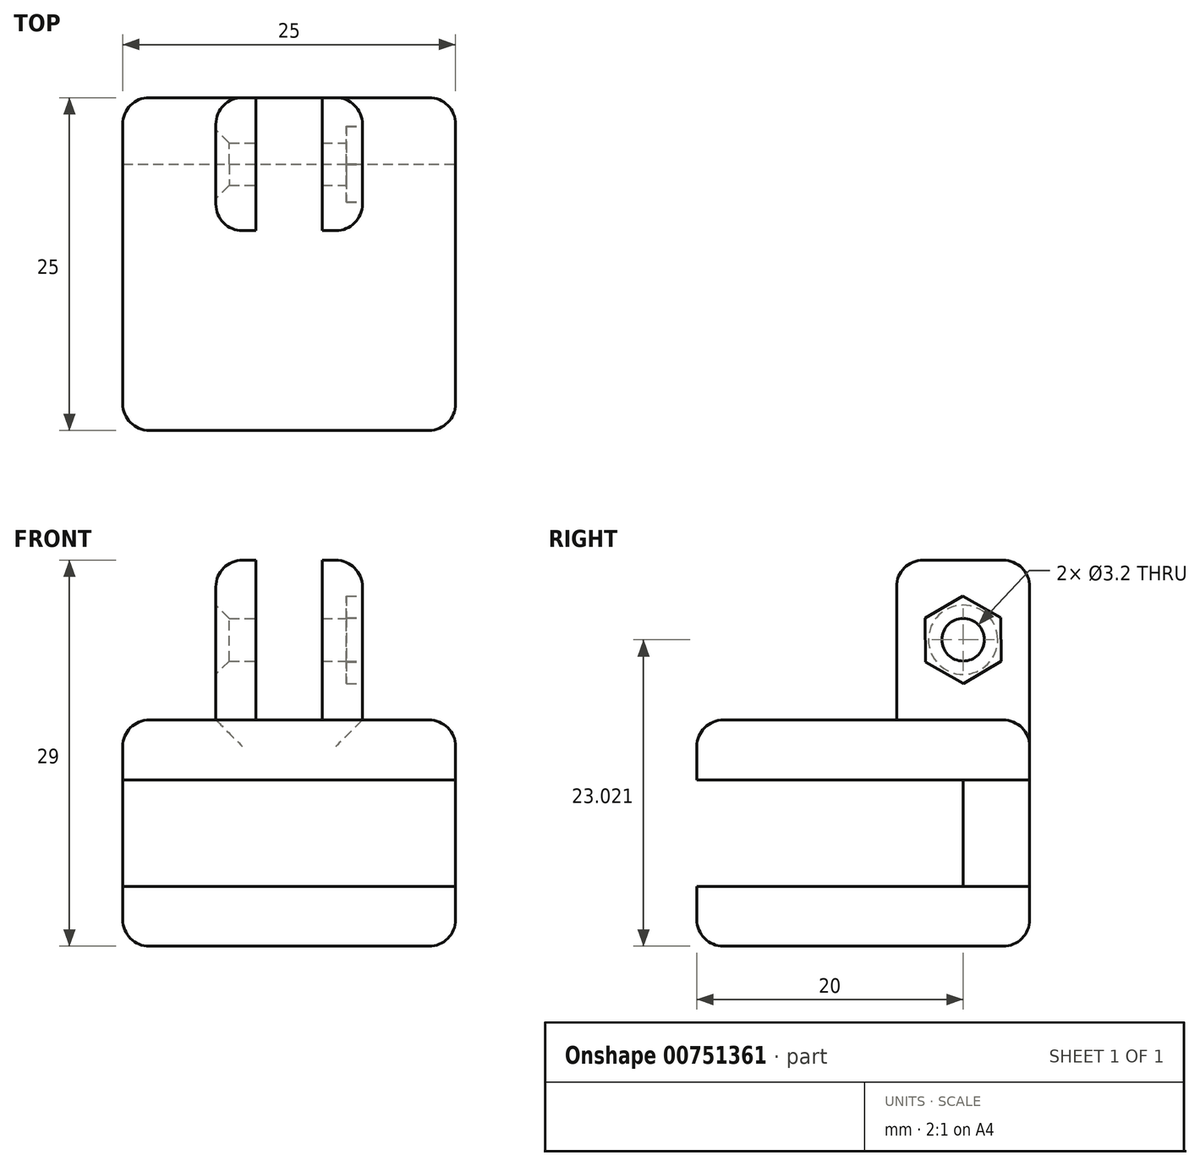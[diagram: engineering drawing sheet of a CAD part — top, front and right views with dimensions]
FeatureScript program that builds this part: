
annotation { "Feature Type Name" : "Feature", "Feature Type Description" : "" }
export const myFeature = defineFeature(function(context is Context, id is Id, definition is map)
    precondition{}
    {
        {
            var Q0;
            Q0=qCreatedBy(makeId("Front.planeOp"),FACE);
            var sketch = newSketch(context, id + "F0", { "sketchPlane" : qUnion([Q0])});
            skLineSegment(sketch, "E0.bottom", {"start": v(12.5, 8.5) * mm, "end": v(-12.5, 8.5) * mm});
            skLineSegment(sketch, "E0.top", {"start": v(12.5, -8.5) * mm, "end": v(-12.5, -8.5) * mm});
            skLineSegment(sketch, "E0.left", {"start": v(12.5, 8.5) * mm, "end": v(12.5, -8.5) * mm});
            skLineSegment(sketch, "E0.right", {"start": v(-12.5, 8.5) * mm, "end": v(-12.5, -8.5) * mm});
            skPoint(sketch, "E0.middle", {"position": v(0, 0) * mm});
            skLineSegment(sketch, "E1.bottom", {"start": v(-2.5, 20.5) * mm, "end": v(2.5, 20.5) * mm});
            skLineSegment(sketch, "E1.top", {"start": v(-2.5, 8.5) * mm, "end": v(2.5, 8.5) * mm});
            skLineSegment(sketch, "E1.left", {"start": v(-2.5, 20.5) * mm, "end": v(-2.5, 8.5) * mm});
            skLineSegment(sketch, "E1.right", {"start": v(2.5, 20.5) * mm, "end": v(2.5, 8.5) * mm});
            skLineSegment(sketch, "E2", {"start": v(0, 0) * mm, "end": v(0, 48.1) * mm, "construction": true});
            skPoint(sketch, "E2.endSnap0", {"position": v(0, 8.5) * mm});
            skLineSegment(sketch, "E3.bottom", {"start": v(-2.5, 8.5) * mm, "end": v(-5.5, 8.5) * mm});
            skLineSegment(sketch, "E3.top", {"start": v(-2.5, 20.5) * mm, "end": v(-5.5, 20.5) * mm});
            skLineSegment(sketch, "E3.left", {"start": v(-2.5, 8.5) * mm, "end": v(-2.5, 20.5) * mm});
            skLineSegment(sketch, "E3.right", {"start": v(-5.5, 8.5) * mm, "end": v(-5.5, 20.5) * mm});
            skLineSegment(sketch, "E4.MirrorCS", {"start": v(5.5, 8.5) * mm, "end": v(5.5, 20.5) * mm});
            skLineSegment(sketch, "E5.MirrorCS", {"start": v(2.5, 20.5) * mm, "end": v(5.5, 20.5) * mm});
            skLineSegment(sketch, "E6.MirrorCS", {"start": v(2.5, 8.5) * mm, "end": v(5.5, 8.5) * mm});
            skPoint(sketch, "E7.visualSharp", {"position": v(-12.5, -8.5) * mm});
            skLineSegment(sketch, "E7.filletArc", {"start": v(-12.5, -8.5) * mm, "end": v(-12.5, -8.5) * mm});
            skPoint(sketch, "E8.visualSharp", {"position": v(12.5, -8.5) * mm});
            skLineSegment(sketch, "E8.filletArc", {"start": v(12.5, -8.5) * mm, "end": v(12.5, -8.5) * mm});
            skPoint(sketch, "E9.visualSharp", {"position": v(-5.5, 20.5) * mm});
            skLineSegment(sketch, "E9.filletArc", {"start": v(-5.5, 20.5) * mm, "end": v(-5.5, 20.5) * mm});
            skPoint(sketch, "E10.visualSharp", {"position": v(5.5, 20.5) * mm});
            skLineSegment(sketch, "E10.filletArc", {"start": v(5.5, 20.5) * mm, "end": v(5.5, 20.5) * mm});
            skLineSegment(sketch, "E11.bottom", {"start": v(-12.5, 4) * mm, "end": v(12.5, 4) * mm});
            skLineSegment(sketch, "E11.top", {"start": v(-12.5, -4) * mm, "end": v(12.5, -4) * mm});
            skLineSegment(sketch, "E11.left", {"start": v(-12.5, 4) * mm, "end": v(-12.5, -4) * mm});
            skLineSegment(sketch, "E11.right", {"start": v(12.5, 4) * mm, "end": v(12.5, -4) * mm});
            skLineSegment(sketch, "E12", {"start": v(-5.5, 20.5) * mm, "end": v(5.5, 8.5) * mm, "construction": true});
            skLineSegment(sketch, "E13", {"start": v(5.5, 20.5) * mm, "end": v(-5.5, 8.5) * mm, "construction": true});
            skPoint(sketch, "E14", {"position": v(0, 14.5) * mm});
            skLineSegment(sketch, "E15", {"start": v(0, 14.5) * mm, "end": v(-5.5, 14.5) * mm, "construction": true});
            skPoint(sketch, "E16", {"position": v(-5.5, 14.5) * mm});
            skSolve(sketch);
        }
        {
            var Q0;
            {var subQ0=sQuery(id+"F0.wireOp",EDGE,"E0.top");Q0=makeQuery(id+"F0.imprint","IMPRINT",FACE,{"disambiguationData":[TD([[makeQuery(id+"F0.imprint","IMPRINT",EDGE,{"derivedFrom":subQ0}),-1.0]])]});}
            var Q1;
            {var subQ9=sQuery(id+"F0.wireOp",EDGE,"E11.bottom");Q1=makeQuery(id+"F0.imprint","IMPRINT",FACE,{"disambiguationData":[TD([[makeQuery(id+"F0.imprint","IMPRINT",EDGE,{"derivedFrom":subQ9}),1.0]])]});}
            extrude(context, id + "F1", {"entities" : qUnion([Q0, Q1]), "depth" : 25 * mm, "offsetDistance" : 25 * mm});
        }
        {
            var Q0;
            {var subQ0=sQuery(id+"F0.wireOp",EDGE,"E11.bottom");Q0=makeQuery(id+"F0.imprint","IMPRINT",FACE,{"disambiguationData":[TD([[makeQuery(id+"F0.imprint","IMPRINT",EDGE,{"derivedFrom":subQ0}),-1.0]])]});}
            extrude(context, id + "F2", {"entities" : qUnion([Q0]), "depth" : 5 * mm, "offsetDistance" : 25 * mm});
        }
        {
            var Q0;
            {var subQ0=sQuery(id+"F0.wireOp",EDGE,"E1.right");Q0=makeQuery(id+"F0.imprint","IMPRINT",FACE,{"disambiguationData":[TD([[makeQuery(id+"F0.imprint","IMPRINT",EDGE,{"derivedFrom":subQ0}),1.0]])]});}
            var Q1;
            {var subQ2=sQuery(id+"F0.wireOp",EDGE,"E1.left");Q1=makeQuery(id+"F0.imprint","IMPRINT",FACE,{"disambiguationData":[TD([[makeQuery(id+"F0.imprint","IMPRINT",EDGE,{"derivedFrom":subQ2}),-1.0]])]});}
            extrude(context, id + "F3", {"entities" : qUnion([Q0, Q1]), "operationType" : NewBodyOperationType.ADD, "depth" : 10 * mm, "offsetDistance" : 25 * mm});
        }
        {
            var Q0;
            Q0=qCreatedBy(makeId("Right.planeOp"),FACE);
            var sketch = newSketch(context, id + "F4", { "sketchPlane" : qUnion([Q0])});
            skLineSegment(sketch, "E17", {"start": v(0, 14.52) * mm, "end": v(-10, 14.52) * mm});
            skCircle(sketch, "E18", {"center": v(-5, 14.52) * mm, "radius": 1.6 * mm});
            skSolve(sketch);
        }
        {
            var Q0;
            {var subQ0=sQuery(id+"F4.wireOp",EDGE,"E18");var subQ1=sQuery(id+"F4.wireOp",EDGE,"E17");var subQ2=makeQuery(id+"F4.imprint","INTERSECT",VERTEX,{"disambiguationData":[OD(0.0)],"derivedFrom":[subQ1,subQ0]});Q0=makeQuery(id+"F4.imprint","IMPRINT",FACE,{"disambiguationData":[TD([[makeQuery(id+"F4.imprint","IMPRINT",EDGE,{"disambiguationData":[TD([[subQ2,1.0]])],"derivedFrom":subQ1}),-1.0]])]});}
            var Q1;
            {var subQ0=sQuery(id+"F4.wireOp",EDGE,"E18");var subQ1=sQuery(id+"F4.wireOp",EDGE,"E17");var subQ2=makeQuery(id+"F4.imprint","INTERSECT",VERTEX,{"disambiguationData":[OD(0.0)],"derivedFrom":[subQ1,subQ0]});Q1=makeQuery(id+"F4.imprint","IMPRINT",FACE,{"disambiguationData":[TD([[makeQuery(id+"F4.imprint","IMPRINT",EDGE,{"disambiguationData":[TD([[subQ2,1.0]])],"derivedFrom":subQ1}),1.0]])]});}
            var Q2;
            Q2=sQuery(id+"F4.wireOp",EDGE,"E18");
            extrude(context, id + "F5", {"entities" : qUnion([Q0, Q1]), "operationType" : NewBodyOperationType.REMOVE, "surfaceEntities" : qUnion([Q2]), "oppositeDirection" : true, "depth" : 11.2 * mm, "offsetDistance" : 25 * mm, "hasSecondDirection" : true, "secondDirectionOppositeDirection" : false, "secondDirectionDepth" : 25 * mm});
        }
        {
            var Q0;
            Q0=makeQuery(id+"F3.opExtrude","SWEPT_EDGE",EDGE,{"disambiguationData":[OSD([sQuery(id+"F0.wireOp",EDGE,"E3.top"),sQuery(id+"F0.wireOp",EDGE,"E3.right")])]});
            var Q1;
            Q1=makeQuery(id+"F1.opExtrude","CAP_EDGE",EDGE,{"disambiguationData":[OSD([sQuery(id+"F0.wireOp",EDGE,"E0.bottom")])],"isStart":false});
            var Q2;
            Q2=makeQuery(id+"F1.opExtrude","SWEPT_EDGE",EDGE,{"disambiguationData":[OSD([sQuery(id+"F0.wireOp",EDGE,"E0.bottom"),sQuery(id+"F0.wireOp",EDGE,"E0.left")])]});
            var Q3;
            Q3=makeQuery(id+"F1.opExtrude","SWEPT_EDGE",EDGE,{"disambiguationData":[OSD([sQuery(id+"F0.wireOp",EDGE,"E0.bottom"),sQuery(id+"F0.wireOp",EDGE,"E0.right")])]});
            var Q4;
            {var subQ0=sQuery(id+"F0.wireOp",EDGE,"E0.right");Q4=makeQuery(id+"F1.opExtrude","CAP_EDGE",EDGE,{"disambiguationData":[OSD([subQ0]),TDD([makeQuery(id+"F0.imprint","IMPRINT",EDGE,{"disambiguationData":[TD([[makeQuery(id+"F0.imprint","INTERSECT",VERTEX,{"derivedFrom":[subQ0,sQuery(id+"F0.wireOp",EDGE,"E11.bottom")]}),1.0]])],"derivedFrom":subQ0})])],"isStart":true});}
            var Q5;
            {var subQ0=sQuery(id+"F0.wireOp",EDGE,"E0.bottom");var subQ3=sQuery(id+"F0.wireOp",EDGE,"E3.right");Q5=makeQuery(id+"F3.boolean.opBoolean","SPLIT",EDGE,{"disambiguationData":[TD([makeQuery(id+"F3.opExtrude","SWEPT_FACE",FACE,{"disambiguationData":[OSD([subQ3])]})])],"derivedFrom":makeQuery(id+"F1.opExtrude","CAP_EDGE",EDGE,{"disambiguationData":[OSD([subQ0])],"isStart":true})});}
            var Q6;
            {var subQ0=sQuery(id+"F0.wireOp",EDGE,"E4.MirrorCS");var subQ1=sQuery(id+"F0.wireOp",EDGE,"E0.bottom");Q6=makeQuery(id+"F3.boolean.opBoolean","SPLIT",EDGE,{"disambiguationData":[TD([makeQuery(id+"F3.opExtrude","SWEPT_FACE",FACE,{"disambiguationData":[OSD([subQ0])]})])],"derivedFrom":makeQuery(id+"F1.opExtrude","CAP_EDGE",EDGE,{"disambiguationData":[OSD([subQ1])],"isStart":true})});}
            var Q7;
            Q7=makeQuery(id+"F2.opExtrude","CAP_EDGE",EDGE,{"disambiguationData":[OSD([sQuery(id+"F0.wireOp",EDGE,"E0.left")])],"isStart":true});
            var Q8;
            {var subQ0=sQuery(id+"F0.wireOp",EDGE,"E0.left");Q8=makeQuery(id+"F1.opExtrude","CAP_EDGE",EDGE,{"disambiguationData":[OSD([subQ0]),TDD([makeQuery(id+"F0.imprint","IMPRINT",EDGE,{"disambiguationData":[TD([[makeQuery(id+"F0.imprint","INTERSECT",VERTEX,{"derivedFrom":[subQ0,sQuery(id+"F0.wireOp",EDGE,"E11.bottom")]}),1.0]])],"derivedFrom":subQ0})])],"isStart":true});}
            var Q9;
            {var subQ0=sQuery(id+"F0.wireOp",EDGE,"E0.left");Q9=makeQuery(id+"F1.opExtrude","CAP_EDGE",EDGE,{"disambiguationData":[OSD([subQ0]),TDD([makeQuery(id+"F0.imprint","IMPRINT",EDGE,{"disambiguationData":[TD([[makeQuery(id+"F0.imprint","INTERSECT",VERTEX,{"derivedFrom":[sQuery(id+"F0.wireOp",EDGE,"E0.top"),subQ0]}),1.0]])],"derivedFrom":subQ0})])],"isStart":true});}
            var Q10;
            Q10=makeQuery(id+"F2.opExtrude","CAP_EDGE",EDGE,{"disambiguationData":[OSD([sQuery(id+"F0.wireOp",EDGE,"E0.right")])],"isStart":true});
            var Q11;
            {var subQ0=sQuery(id+"F0.wireOp",EDGE,"E0.right");Q11=makeQuery(id+"F1.opExtrude","CAP_EDGE",EDGE,{"disambiguationData":[OSD([subQ0]),TDD([makeQuery(id+"F0.imprint","IMPRINT",EDGE,{"disambiguationData":[TD([[makeQuery(id+"F0.imprint","INTERSECT",VERTEX,{"derivedFrom":[sQuery(id+"F0.wireOp",EDGE,"E0.top"),subQ0]}),1.0]])],"derivedFrom":subQ0})])],"isStart":true});}
            var Q12;
            Q12=makeQuery(id+"F1.opExtrude","CAP_EDGE",EDGE,{"disambiguationData":[OSD([sQuery(id+"F0.wireOp",EDGE,"E0.top")])],"isStart":true});
            var Q13;
            Q13=makeQuery(id+"F1.opExtrude","SWEPT_EDGE",EDGE,{"disambiguationData":[OSD([sQuery(id+"F0.wireOp",EDGE,"E0.top"),sQuery(id+"F0.wireOp",EDGE,"E0.right")])]});
            var Q14;
            Q14=makeQuery(id+"F1.opExtrude","SWEPT_EDGE",EDGE,{"disambiguationData":[OSD([sQuery(id+"F0.wireOp",EDGE,"E0.top"),sQuery(id+"F0.wireOp",EDGE,"E0.left")])]});
            var Q15;
            Q15=makeQuery(id+"F3.opExtrude","CAP_EDGE",EDGE,{"disambiguationData":[OSD([sQuery(id+"F0.wireOp",EDGE,"E3.right")])],"isStart":true});
            var Q16;
            Q16=makeQuery(id+"F3.opExtrude","CAP_EDGE",EDGE,{"disambiguationData":[OSD([sQuery(id+"F0.wireOp",EDGE,"E3.right")])],"isStart":false});
            var Q17;
            Q17=makeQuery(id+"F3.opExtrude","CAP_EDGE",EDGE,{"disambiguationData":[OSD([sQuery(id+"F0.wireOp",EDGE,"E4.MirrorCS")])],"isStart":true});
            var Q18;
            Q18=makeQuery(id+"F3.opExtrude","CAP_EDGE",EDGE,{"disambiguationData":[OSD([sQuery(id+"F0.wireOp",EDGE,"E4.MirrorCS")])],"isStart":false});
            var Q19;
            {var subQ0=sQuery(id+"F0.wireOp",EDGE,"E0.left");Q19=makeQuery(id+"F1.opExtrude","CAP_EDGE",EDGE,{"disambiguationData":[OSD([subQ0]),TDD([makeQuery(id+"F0.imprint","IMPRINT",EDGE,{"disambiguationData":[TD([[makeQuery(id+"F0.imprint","INTERSECT",VERTEX,{"derivedFrom":[subQ0,sQuery(id+"F0.wireOp",EDGE,"E11.bottom")]}),1.0]])],"derivedFrom":subQ0})])],"isStart":false});}
            var Q20;
            {var subQ0=sQuery(id+"F0.wireOp",EDGE,"E0.right");Q20=makeQuery(id+"F1.opExtrude","CAP_EDGE",EDGE,{"disambiguationData":[OSD([subQ0]),TDD([makeQuery(id+"F0.imprint","IMPRINT",EDGE,{"disambiguationData":[TD([[makeQuery(id+"F0.imprint","INTERSECT",VERTEX,{"derivedFrom":[subQ0,sQuery(id+"F0.wireOp",EDGE,"E11.bottom")]}),1.0]])],"derivedFrom":subQ0})])],"isStart":false});}
            var Q21;
            Q21=makeQuery(id+"F1.opExtrude","CAP_EDGE",EDGE,{"disambiguationData":[OSD([sQuery(id+"F0.wireOp",EDGE,"E0.top")])],"isStart":false});
            var Q22;
            {var subQ0=sQuery(id+"F0.wireOp",EDGE,"E0.right");Q22=makeQuery(id+"F1.opExtrude","CAP_EDGE",EDGE,{"disambiguationData":[OSD([subQ0]),TDD([makeQuery(id+"F0.imprint","IMPRINT",EDGE,{"disambiguationData":[TD([[makeQuery(id+"F0.imprint","INTERSECT",VERTEX,{"derivedFrom":[sQuery(id+"F0.wireOp",EDGE,"E0.top"),subQ0]}),1.0]])],"derivedFrom":subQ0})])],"isStart":false});}
            var Q23;
            {var subQ0=sQuery(id+"F0.wireOp",EDGE,"E0.left");Q23=makeQuery(id+"F1.opExtrude","CAP_EDGE",EDGE,{"disambiguationData":[OSD([subQ0]),TDD([makeQuery(id+"F0.imprint","IMPRINT",EDGE,{"disambiguationData":[TD([[makeQuery(id+"F0.imprint","INTERSECT",VERTEX,{"derivedFrom":[sQuery(id+"F0.wireOp",EDGE,"E0.top"),subQ0]}),1.0]])],"derivedFrom":subQ0})])],"isStart":false});}
            var Q24;
            Q24=makeQuery(id+"F3.opExtrude","SWEPT_EDGE",EDGE,{"disambiguationData":[OSD([sQuery(id+"F0.wireOp",EDGE,"E4.MirrorCS"),sQuery(id+"F0.wireOp",EDGE,"E5.MirrorCS")])]});
            var Q25;
            Q25=makeQuery(id+"F3.opExtrude","CAP_EDGE",EDGE,{"disambiguationData":[OSD([sQuery(id+"F0.wireOp",EDGE,"E5.MirrorCS")])],"isStart":false});
            var Q26;
            Q26=makeQuery(id+"F3.opExtrude","CAP_EDGE",EDGE,{"disambiguationData":[OSD([sQuery(id+"F0.wireOp",EDGE,"E5.MirrorCS")])],"isStart":true});
            var Q27;
            Q27=makeQuery(id+"F3.opExtrude","CAP_EDGE",EDGE,{"disambiguationData":[OSD([sQuery(id+"F0.wireOp",EDGE,"E3.top")])],"isStart":true});
            var Q28;
            Q28=makeQuery(id+"F3.opExtrude","CAP_EDGE",EDGE,{"disambiguationData":[OSD([sQuery(id+"F0.wireOp",EDGE,"E3.top")])],"isStart":false});
            fillet(context, id + "F6", {"entities" : qUnion([Q0, Q1, Q2, Q3, Q4, Q5, Q6, Q7, Q8, Q9, Q10, Q11, Q12, Q13, Q14, Q15, Q16, Q17, Q18, Q19, Q20, Q21, Q22, Q23, Q24, Q25, Q26, Q27, Q28]), "radius" : 2 * mm, "tangentPropagation" : true, "allowEdgeOverflow" : false});
        }
        {
            var Q0;
            Q0=makeQuery(id+"F5.boolean.opBoolean","INTERSECT",EDGE,{"derivedFrom":[makeQuery(id+"F3.opExtrude","SWEPT_FACE",FACE,{"disambiguationData":[OSD([sQuery(id+"F0.wireOp",EDGE,"E3.right")])]}),makeQuery(id+"F5.opExtrude","SWEPT_FACE",FACE,{"disambiguationData":[OSD([sQuery(id+"F4.wireOp",EDGE,"E18")])]})]});
            chamfer(context, id + "F7", {"entities" : qUnion([Q0]), "width" : 1 * mm, "tangentPropagation" : true});
        }
        {
            var Q0;
            Q0=makeQuery(id+"F3.opExtrude","SWEPT_FACE",FACE,{"disambiguationData":[OSD([sQuery(id+"F0.wireOp",EDGE,"E4.MirrorCS")])]});
            var sketch = newSketch(context, id + "F8", { "sketchPlane" : qUnion([Q0])});
            skCircle(sketch, "E19.cCircle", {"center": v(-5, 14.52) * mm, "radius": 2.85 * mm, "construction": true});
            skLineSegment(sketch, "E19.0", {"start": v(-7.86, 16.14) * mm, "end": v(-5.03, 17.81) * mm});
            skLineSegment(sketch, "E19.1", {"start": v(-5.03, 17.81) * mm, "end": v(-2.16, 16.19) * mm});
            skLineSegment(sketch, "E19.2", {"start": v(-2.16, 16.19) * mm, "end": v(-2.14, 12.9) * mm});
            skLineSegment(sketch, "E19.3", {"start": v(-2.14, 12.9) * mm, "end": v(-4.97, 11.23) * mm});
            skLineSegment(sketch, "E19.4", {"start": v(-4.97, 11.23) * mm, "end": v(-7.84, 12.85) * mm});
            skLineSegment(sketch, "E19.5", {"start": v(-7.84, 12.85) * mm, "end": v(-7.86, 16.14) * mm});
            skPoint(sketch, "E19.0.midPoint", {"position": v(-6.45, 16.98) * mm});
            skSolve(sketch);
        }
        {
            var Q0;
            Q0 = qSketchRegion(id + "F8", true);
            extrude(context, id + "F9", {"entities" : qUnion([Q0]), "operationType" : NewBodyOperationType.REMOVE, "oppositeDirection" : true, "depth" : 1.2 * mm, "offsetDistance" : 25 * mm});
        }
    });
